# Revit family: ВВГ_ВВГФ
name_source: partatom
category: Арматура воздуховодов
units: mm (PartAtom-declared; Revit-internal decimal feet)

## family parameters
Всегда вертикально = Да
На основе рабочей плоскости = Нет
Общий = Нет
При загрузке вырезать с полостями = Нет
Размер круглого соединителя = Использовать диаметр
Тип детали = Присоединяется

## types (25) — shared parameters
00_20_Виробник = Вентс
00_20_Назва = Гнучка віброгасильна вставка
URL = https://vents.ua
n = 12
Изготовитель = Вентс
Класифікація навантаження = HVAC
Максимальний потік повітря = 0.0 л/с
Матеріал зони обслуговування = <По категории>
Матеріал корпусу = Сталь, гальванізована
Повітряний потік = 0.0 л/с
Статичний тиск повітря = 0.0 Па
Температура повітря, що переміщається = -40...+80 °С
zero-valued in all types: Отметка по умолчанию

## per-type parameters (varying)
| type | D | D1 | D2 | Dn | L | R1 | d | l | l1 | l2 | t | Вага | Довжина | Діаметр | Фланец |
| ВВГФ-400 | 412 мм | 438 мм | 465 мм | 417 мм | 160 мм | 219 мм | 8 мм | 80 мм | 53 мм | 53 мм | 155 мм | 2.57 кг | 160 мм | 465 мм | Да |
| ВВГФ-450 | 462 мм | 487 мм | 515 мм | 467 мм | 160 мм | 244 мм | 8 мм | 80 мм | 53 мм | 53 мм | 155 мм | 2.88 кг | 160 мм | 515 мм | Да |
| ВВГФ-500 | 515 мм | 541 мм | 570 мм | 520 мм | 160 мм | 271 мм | 12 мм | 80 мм | 53 мм | 53 мм | 155 мм | 3.81 кг | 160 мм | 570 мм | Да |
| ВВГФ-550 | 565 мм | 605 мм | 636 мм | 570 мм | 160 мм | 303 мм | 12 мм | 80 мм | 53 мм | 53 мм | 155 мм | 4.53 кг | 160 мм | 636 мм | Да |
| ВВГФ-630 | 645 мм | 674 мм | 715 мм | 650 мм | 160 мм | 337 мм | 12 мм | 80 мм | 53 мм | 53 мм | 155 мм | 5.13 кг | 160 мм | 715 мм | Да |
| ВВГФ 350 | 362 мм | 395 мм | 421 мм | 367 мм | 160 мм | 198 мм | 8 мм | 80 мм | 53 мм | 53 мм | 155 мм | 2.06 кг | 160 мм | 421 мм | Да |
| ВВГФ 200 | 205 мм | 235 мм | 255 мм | 210 мм | 160 мм | 118 мм | 8 мм | 80 мм | 53 мм | 53 мм | 155 мм | 1.29 кг | 160 мм | 255 мм | Да |
| ВВГФ 250 | 260 мм | 286 мм | 306 мм | 265 мм | 160 мм | 143 мм | 8 мм | 80 мм | 53 мм | 53 мм | 155 мм | 1.21 кг | 160 мм | 306 мм | Да |
| ВВГФ 300 | 310 мм | 356 мм | 382 мм | 315 мм | 160 мм | 178 мм | 8 мм | 80 мм | 53 мм | 53 мм | 155 мм | 1.90 кг | 160 мм | 382 мм | Да |
| ВВГ 100 | 101 мм | 235 мм | 255 мм | 106 мм | 130 мм | 118 мм | 8 мм | 65 мм | 87 мм | 22 мм | 125 мм | 0.14 кг | 130 мм | 255 мм | Нет |
| ВВГ 125 | 126 мм | 235 мм | 255 мм | 131 мм | 130 мм | 118 мм | 8 мм | 65 мм | 87 мм | 22 мм | 125 мм | 0.17 кг | 130 мм | 255 мм | Нет |
| ВВГ 140 | 140 мм | 235 мм | 255 мм | 145 мм | 130 мм | 118 мм | 8 мм | 65 мм | 87 мм | 22 мм | 125 мм | 0.21 кг | 130 мм | 255 мм | Нет |
| ВВГ 150 | 151 мм | 235 мм | 255 мм | 156 мм | 130 мм | 118 мм | 8 мм | 65 мм | 87 мм | 22 мм | 125 мм | 0.21 кг | 130 мм | 255 мм | Нет |
| ВВГ 160 | 161 мм | 235 мм | 255 мм | 166 мм | 130 мм | 118 мм | 8 мм | 65 мм | 87 мм | 22 мм | 125 мм | 0.22 кг | 130 мм | 255 мм | Нет |
| ВВГ 180 | 180 мм | 235 мм | 255 мм | 185 мм | 130 мм | 118 мм | 8 мм | 65 мм | 87 мм | 22 мм | 125 мм | 0.26 кг | 130 мм | 255 мм | Нет |
| ВВГ 200 | 201 мм | 235 мм | 255 мм | 206 мм | 130 мм | 118 мм | 8 мм | 65 мм | 87 мм | 22 мм | 125 мм | 0.28 кг | 130 мм | 255 мм | Нет |
| ВВГ 225 | 223 мм | 235 мм | 255 мм | 228 мм | 130 мм | 118 мм | 8 мм | 65 мм | 87 мм | 22 мм | 125 мм | 0.31 кг | 130 мм | 255 мм | Нет |
| ВВГ 240 | 239 мм | 286 мм | 306 мм | 244 мм | 130 мм | 143 мм | 8 мм | 65 мм | 87 мм | 22 мм | 125 мм | 0.34 кг | 130 мм | 306 мм | Нет |
| ВВГ 250 | 251 мм | 286 мм | 306 мм | 256 мм | 130 мм | 143 мм | 8 мм | 65 мм | 87 мм | 22 мм | 125 мм | 0.35 кг | 130 мм | 306 мм | Нет |
| ВВГ 280 | 280 мм | 286 мм | 306 мм | 285 мм | 130 мм | 143 мм | 8 мм | 65 мм | 87 мм | 22 мм | 125 мм | 0.38 кг | 130 мм | 306 мм | Нет |
| ВВГ 315 | 316 мм | 356 мм | 382 мм | 321 мм | 130 мм | 178 мм | 8 мм | 65 мм | 87 мм | 22 мм | 125 мм | 0.44 кг | 130 мм | 382 мм | Нет |
| ВВГ 355 | 356 мм | 356 мм | 382 мм | 361 мм | 130 мм | 178 мм | 8 мм | 65 мм | 87 мм | 22 мм | 125 мм | 0.50 кг | 130 мм | 382 мм | Нет |
| ВВГ 400 | 401 мм | 438 мм | 465 мм | 406 мм | 130 мм | 219 мм | 8 мм | 65 мм | 87 мм | 22 мм | 125 мм | 0.56 кг | 130 мм | 465 мм | Нет |
| ВВГ 450 | 451 мм | 487 мм | 515 мм | 456 мм | 130 мм | 244 мм | 8 мм | 65 мм | 87 мм | 22 мм | 125 мм | 0.64 кг | 130 мм | 515 мм | Нет |
| ВВГ 500 | 501 мм | 541 мм | 570 мм | 506 мм | 130 мм | 271 мм | 12 мм | 65 мм | 87 мм | 22 мм | 125 мм | 0.71 кг | 130 мм | 570 мм | Нет |

note: column(s) folded — value = type name in every type: 00_20_Тип
